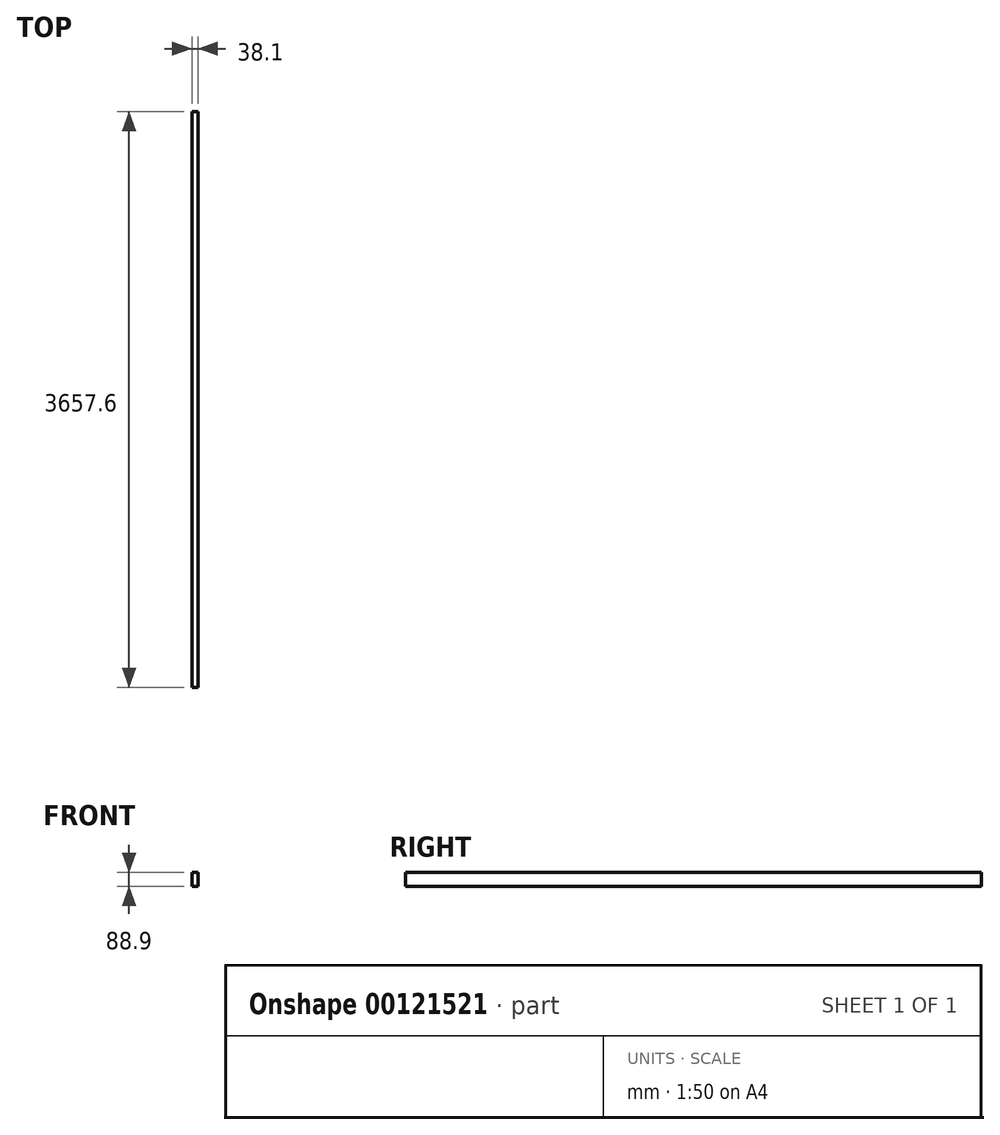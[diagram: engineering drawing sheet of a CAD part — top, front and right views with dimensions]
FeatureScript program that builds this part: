
annotation { "Feature Type Name" : "Feature", "Feature Type Description" : "" }
export const myFeature = defineFeature(function(context is Context, id is Id, definition is map)
    precondition{}
    {
        {
            var Q0;
            Q0=qCreatedBy(makeId("Front.planeOp"),FACE);
            var sketch = newSketch(context, id + "F0", { "sketchPlane" : qUnion([Q0])});
            skLineSegment(sketch, "E0.bottom", {"start": v(-38.1, -44.45) * mm, "end": v(0, -44.45) * mm});
            skLineSegment(sketch, "E0.top", {"start": v(-38.1, 44.45) * mm, "end": v(0, 44.45) * mm});
            skLineSegment(sketch, "E0.left", {"start": v(-38.1, -44.45) * mm, "end": v(-38.1, 44.45) * mm});
            skLineSegment(sketch, "E0.right", {"start": v(0, -44.45) * mm, "end": v(0, 44.45) * mm});
            skSolve(sketch);
        }
        {
            var Q0;
            Q0=makeQuery(id+"F0.imprint","IMPRINT",FACE,{"disambiguationData":[TD([[makeQuery(id+"F0.imprint","IMPRINT",EDGE,{"derivedFrom":sQuery(id+"F0.wireOp",EDGE,"E0.bottom")}),1.0]])]});
            extrude(context, id + "F1", {"entities" : qUnion([Q0]), "flatOperationType" : FlatOperationType.REMOVE, "offsetDistance" : 25.4 * mm, "depth" : 3657.6 * mm, "domain" : OperationDomain.MODEL});
        }
    });
